# Revit family: Pump_Commercial-Effluent-Zoeller-267_Non_Automatic_Series
name_source: partatom
category: Mechanical Equipment
revit_build: Autodesk Revit 2014 (Build: 20130308_1515(x64)
units: mm (PartAtom-declared; Revit-internal decimal feet)

## types (6) — shared parameters
Assembly Code = D2010900
Cooling = Oil Filled
Cord Length = 180"
Cord Type = UL listed, neoprene
Default Elevation = 0"
Description = Non-Automatic Submersible sewage/effluent or dewatering pump.
Discharge Diameter = 2" NPT
Discharge Height = 6 7/16"
Discharge Radius = 1"
Height = 14 5/16"
Hertz = 60
Impeller Type = Non-clogging vortex
Installation Type = Floor Mounted
Insulation = Class B
Length = 13 1/16"
Manufacturer = Zoeller
Material = Cast Iron-Zoeller-Powder Coated Epoxy
Max. Flow at Min. Head = 115 GPM @ 5'
Max. Water Temp. = 130 °F
Maximum Head = 246"
Model = 267
Motor = 1/2 HP
Motor Thermal Shutoff = Auto Reset Thermal Overload (1 Ph).
Motor Type = Submersible
O-Rings and Cover Gasket = Neoprene
Operation = Non-Automatic
Price = Prices may vary. Please consult Manufacturer Representative for most up-to-date price list.
Product Page URL = http://www.zoellerpumps.com
RPM = 1725
Revised Date = 2/22/2016
Shaft Seal = Carbon and Ceramic
Shipping Weight = 47.50 lb
Solid Handling = 2"
Type = Split Phase or 3 Ph
URL = http://www.zoellerpumps.com
Warranty Information = 36 Months (Limited)
Waste Connection = Yes
Width = 11 1/32"

## per-type parameters (varying)
| type | Amps | Apparent Load | Phase | Voltage |
| N267 - 115V 1Ph | 10 A | 1196 VA | 1 | 115 V |
| E267 - 230V 1Ph | 6 A | 1265 VA | 1 | 230 V |
| I267 - 200-208V 1Ph | 6 A | 1240 VA | 1 | 200 V |
| J267 - 200-208V 3Ph | 3 A | 520 VA | 3 | 200 V |
| F267 - 230V 3Ph | 3 A | 598 VA | 3 | 230 V |
| G267 - 460V 3Ph | 2 A | 173 VA | 3 | 115 V |

## geometry (parser evidence)
native form markers: Sweep x3
no freeform markers — native parametric forms only
